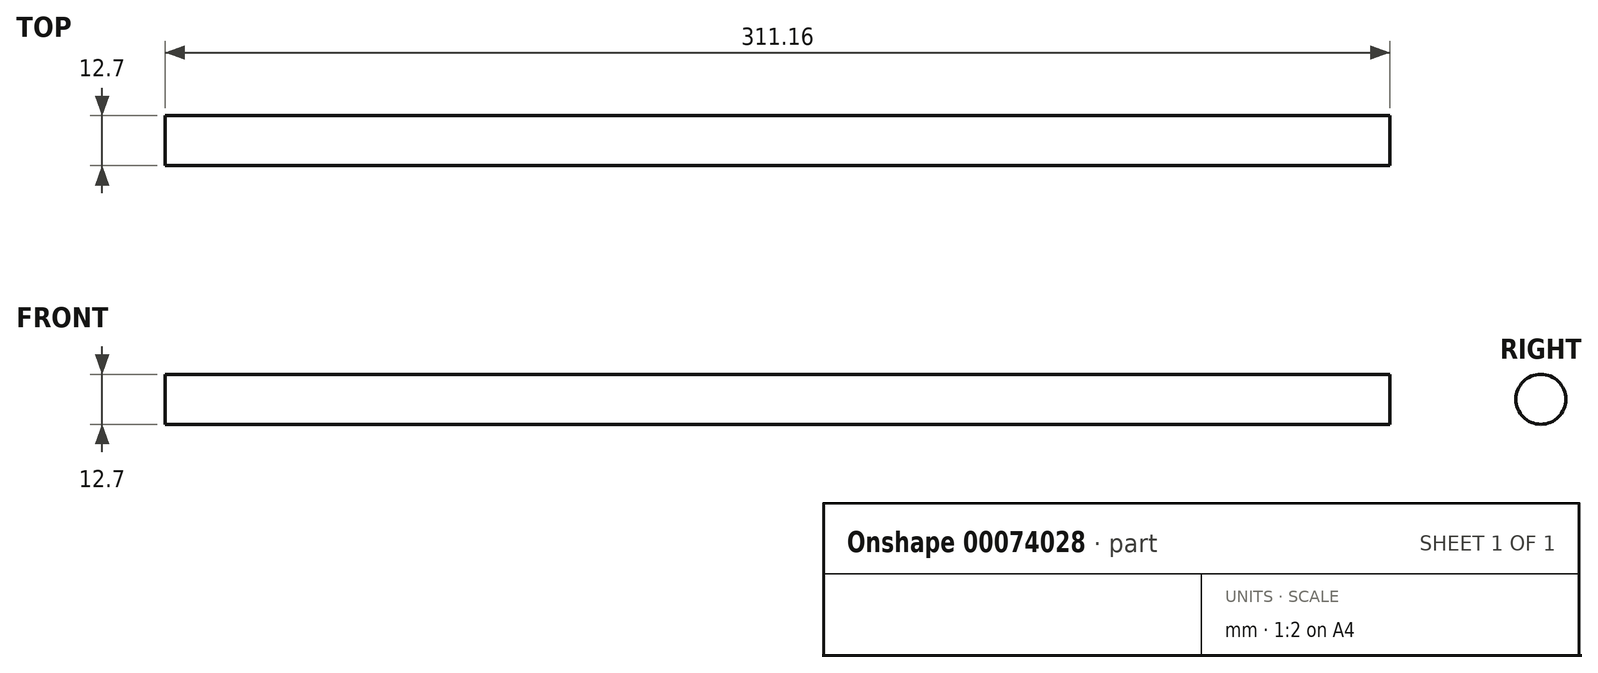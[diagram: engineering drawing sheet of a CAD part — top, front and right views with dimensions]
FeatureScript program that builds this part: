
annotation { "Feature Type Name" : "Feature", "Feature Type Description" : "" }
export const myFeature = defineFeature(function(context is Context, id is Id, definition is map)
    precondition{}
    {
        {
            var Q0;
            Q0=qCreatedBy(makeId("Right.planeOp"),FACE);
            var sketch = newSketch(context, id + "F0", { "sketchPlane" : qUnion([Q0])});
            skCircle(sketch, "E0", {"center": v(0, 0) * mm, "radius": 6.35 * mm});
            skSolve(sketch);
        }
        {
            var Q0;
            Q0=makeQuery(id+"F0.imprint","IMPRINT",FACE,{"disambiguationData":[TD([[makeQuery(id+"F0.imprint","IMPRINT",EDGE,{"derivedFrom":sQuery(id+"F0.wireOp",EDGE,"E0")}),1.0]])]});
            extrude(context, id + "F1", {"entities" : qUnion([Q0]), "depth" : 311.15 * mm, "symmetric" : true});
        }
    });
